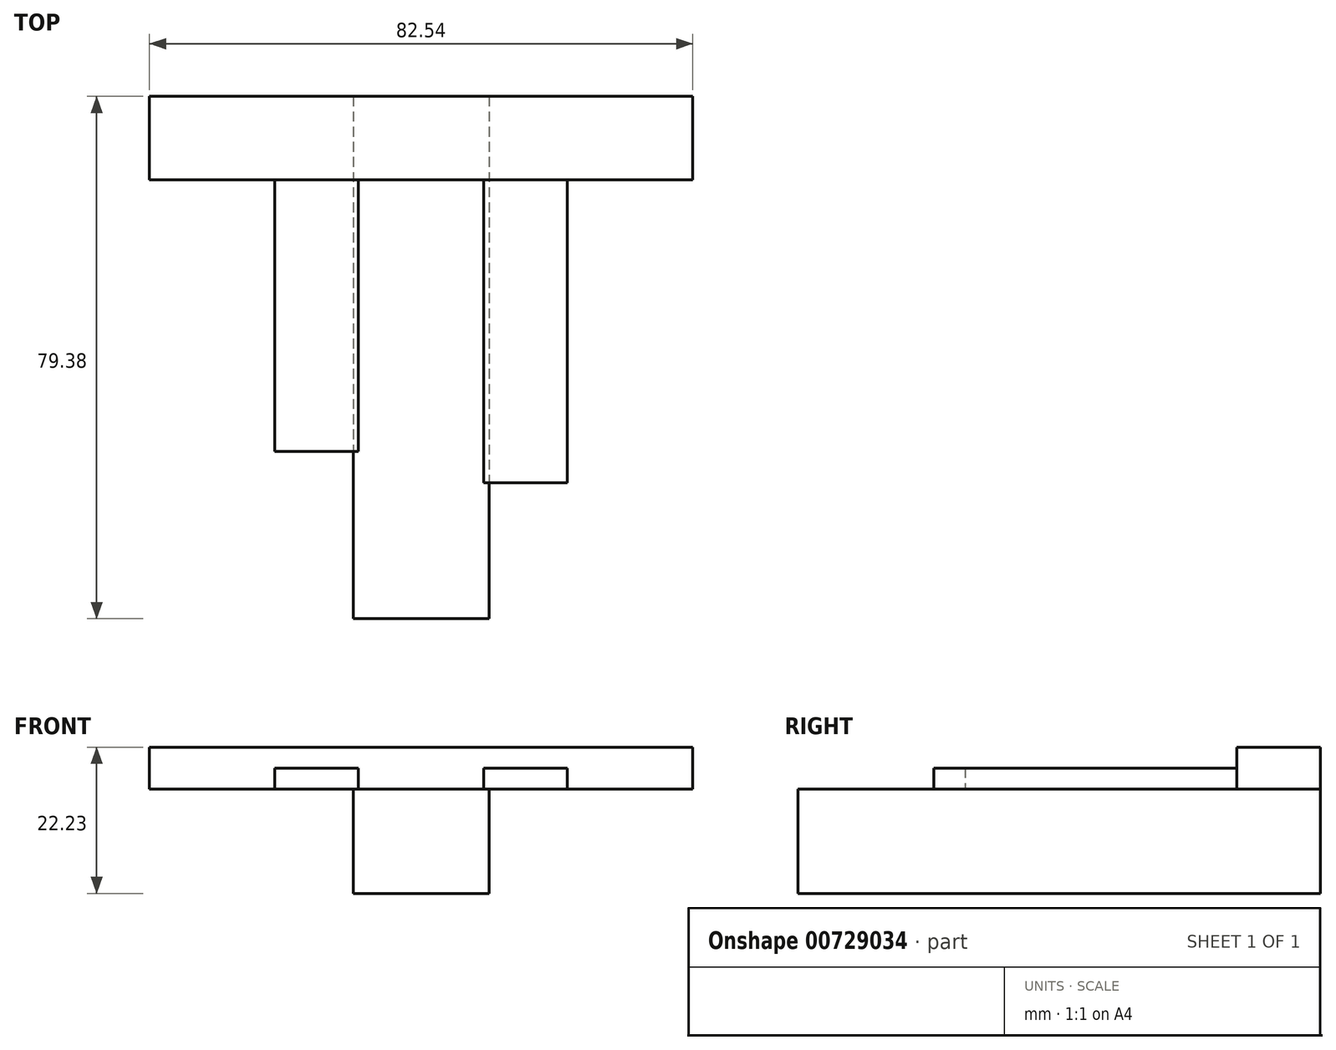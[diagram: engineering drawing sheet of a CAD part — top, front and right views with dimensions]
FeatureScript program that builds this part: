
annotation { "Feature Type Name" : "Feature", "Feature Type Description" : "" }
export const myFeature = defineFeature(function(context is Context, id is Id, definition is map)
    precondition{}
    {
        {
            var Q0;
            Q0=qCreatedBy(makeId("Top.planeOp"),FACE);
            var sketch = newSketch(context, id + "F0", { "sketchPlane" : qUnion([Q0])});
            skLineSegment(sketch, "E0", {"start": v(-41.28, 79.38) * mm, "end": v(41.28, 79.38) * mm});
            skLineSegment(sketch, "E1", {"start": v(41.28, 79.38) * mm, "end": v(41.28, 66.67) * mm});
            skLineSegment(sketch, "E2", {"start": v(41.28, 66.67) * mm, "end": v(-41.28, 66.67) * mm});
            skLineSegment(sketch, "E3", {"start": v(-41.27, 66.67) * mm, "end": v(-41.28, 79.38) * mm});
            skLineSegment(sketch, "E4", {"start": v(0, 0) * mm, "end": v(0, 66.67) * mm, "construction": true});
            skSolve(sketch);
        }
        {
            var Q0;
            Q0 = qSketchRegion(id + "F0", true);
            extrude(context, id + "F1", {"entities" : qUnion([Q0]), "depth" : 6.35 * mm, "offsetDistance" : 25.4 * mm});
        }
        {
            var Q0;
            Q0=makeQuery(id+"F1.opExtrude","CAP_FACE",FACE,{"disambiguationData":[OSD([sQuery(id+"F0.wireOp",EDGE,"E0"),sQuery(id+"F0.wireOp",EDGE,"E1"),sQuery(id+"F0.wireOp",EDGE,"E2"),sQuery(id+"F0.wireOp",EDGE,"E3")])],"isStart":true});
            var sketch = newSketch(context, id + "F2", { "sketchPlane" : qUnion([Q0])});
            skLineSegment(sketch, "E5.bottom", {"start": v(-10.32, -79.38) * mm, "end": v(10.32, -79.38) * mm, "construction": true});
            skLineSegment(sketch, "E5.top", {"start": v(-10.32, 0) * mm, "end": v(10.32, 0) * mm, "construction": true});
            skLineSegment(sketch, "E5.left", {"start": v(-10.32, -79.38) * mm, "end": v(-10.32, 0) * mm, "construction": true});
            skLineSegment(sketch, "E5.right", {"start": v(10.32, -79.38) * mm, "end": v(10.32, 0) * mm, "construction": true});
            skLineSegment(sketch, "E6", {"start": v(0, 0) * mm, "end": v(0, 0) * mm});
            skLineSegment(sketch, "E7.bottom", {"start": v(-22.23, -79.38) * mm, "end": v(-9.53, -79.38) * mm});
            skLineSegment(sketch, "E7.top", {"start": v(-22.23, -25.4) * mm, "end": v(-9.53, -25.4) * mm});
            skLineSegment(sketch, "E7.left", {"start": v(-22.23, -79.38) * mm, "end": v(-22.23, -25.4) * mm});
            skLineSegment(sketch, "E7.right", {"start": v(-9.53, -79.38) * mm, "end": v(-9.53, -25.4) * mm});
            skLineSegment(sketch, "E8.bottom", {"start": v(22.23, -79.38) * mm, "end": v(9.52, -79.38) * mm});
            skLineSegment(sketch, "E8.top", {"start": v(22.22, -20.64) * mm, "end": v(9.52, -20.64) * mm});
            skLineSegment(sketch, "E8.left", {"start": v(22.23, -79.38) * mm, "end": v(22.22, -20.64) * mm});
            skLineSegment(sketch, "E8.right", {"start": v(9.52, -79.38) * mm, "end": v(9.52, -20.64) * mm});
            skSolve(sketch);
        }
        {
            var Q0;
            Q0 = qSketchRegion(id + "F2", true);
            extrude(context, id + "F3", {"entities" : qUnion([Q0]), "operationType" : NewBodyOperationType.ADD, "oppositeDirection" : true, "depth" : 3.17 * mm, "offsetDistance" : 25.4 * mm});
        }
        {
            var Q0;
            Q0=makeQuery(id+"F3.boolean.opBoolean","MERGE",FACE,{"derivedFrom":[makeQuery(id+"F1.opExtrude","CAP_FACE",FACE,{"disambiguationData":[OSD([sQuery(id+"F0.wireOp",EDGE,"E0"),sQuery(id+"F0.wireOp",EDGE,"E1"),sQuery(id+"F0.wireOp",EDGE,"E2"),sQuery(id+"F0.wireOp",EDGE,"E3")])],"isStart":true}),makeQuery(id+"F3.opExtrude","CAP_FACE",FACE,{"disambiguationData":[OSD([sQuery(id+"F2.wireOp",EDGE,"E7.bottom"),sQuery(id+"F2.wireOp",EDGE,"E7.top"),sQuery(id+"F2.wireOp",EDGE,"E7.left"),sQuery(id+"F2.wireOp",EDGE,"E7.right")])],"isStart":true}),makeQuery(id+"F3.opExtrude","CAP_FACE",FACE,{"disambiguationData":[OSD([sQuery(id+"F2.wireOp",EDGE,"E8.bottom"),sQuery(id+"F2.wireOp",EDGE,"E8.top"),sQuery(id+"F2.wireOp",EDGE,"E8.left"),sQuery(id+"F2.wireOp",EDGE,"E8.right")])],"isStart":true})]});
            var sketch = newSketch(context, id + "F4", { "sketchPlane" : qUnion([Q0])});
            skLineSegment(sketch, "E9.bottom", {"start": v(10.32, -79.38) * mm, "end": v(-10.32, -79.38) * mm});
            skLineSegment(sketch, "E9.top", {"start": v(10.32, 0) * mm, "end": v(-10.32, 0) * mm});
            skLineSegment(sketch, "E9.left", {"start": v(10.32, -79.38) * mm, "end": v(10.32, 0) * mm});
            skLineSegment(sketch, "E9.right", {"start": v(-10.32, -79.38) * mm, "end": v(-10.32, 0) * mm});
            skLineSegment(sketch, "E10", {"start": v(0, -79.38) * mm, "end": v(0, -79.38) * mm});
            skSolve(sketch);
        }
        {
            var Q0;
            Q0 = qSketchRegion(id + "F4", true);
            extrude(context, id + "F5", {"entities" : qUnion([Q0]), "operationType" : NewBodyOperationType.ADD, "depth" : 15.88 * mm, "offsetDistance" : 25.4 * mm});
        }
    });
